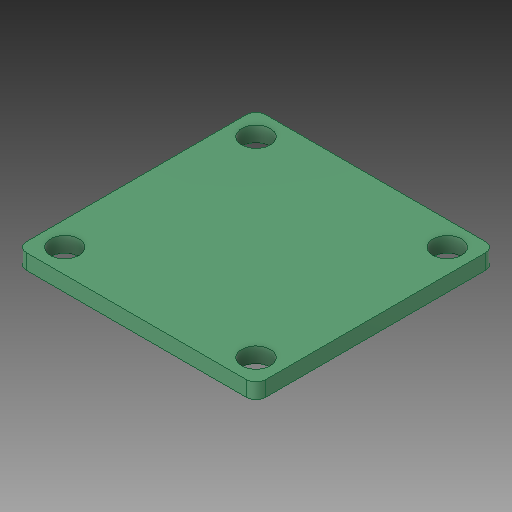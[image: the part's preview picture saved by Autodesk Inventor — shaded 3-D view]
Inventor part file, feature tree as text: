
AUTODESK INVENTOR PART (.ipt)
format: ipt  version: 2018 (Build 220112000, 112)  size: 111,616 bytes
history: native  units: mm
features: sketch x1, extrude x1, hole x1, fillet x1
ambient origin geometry x8: Origin, YZ Plane, XZ Plane, XY Plane, X Axis, Y Axis, Z Axis, Center Point
bodies: Solid1 (feature_tree)
feature tree (4):
  sketch  "Sketch1"  dims[d0=25.0mm d1=25.0mm d2=20.0mm d3=20.0mm d4=2.5mm d5=2.5mm d6=1.6mm d7=0.0mm d8=3.0mm d9=6.0mm d10=4.0mm d11=2.0mm d12=90.0deg d13=8.0mm d14=20.594885mm d15=1.0mm]
  extrude  "Extrusion1"  Depth=25.0mm
  hole  "Hole1"  [1 undecoded]
  fillet  "Fillet1"  Radius=20.0mm
note: 1 required parameter value undecoded (feature->parameter linkage not recoverable at this tier; creation-order binding heuristic only, values carry confidence <= 0.55)
